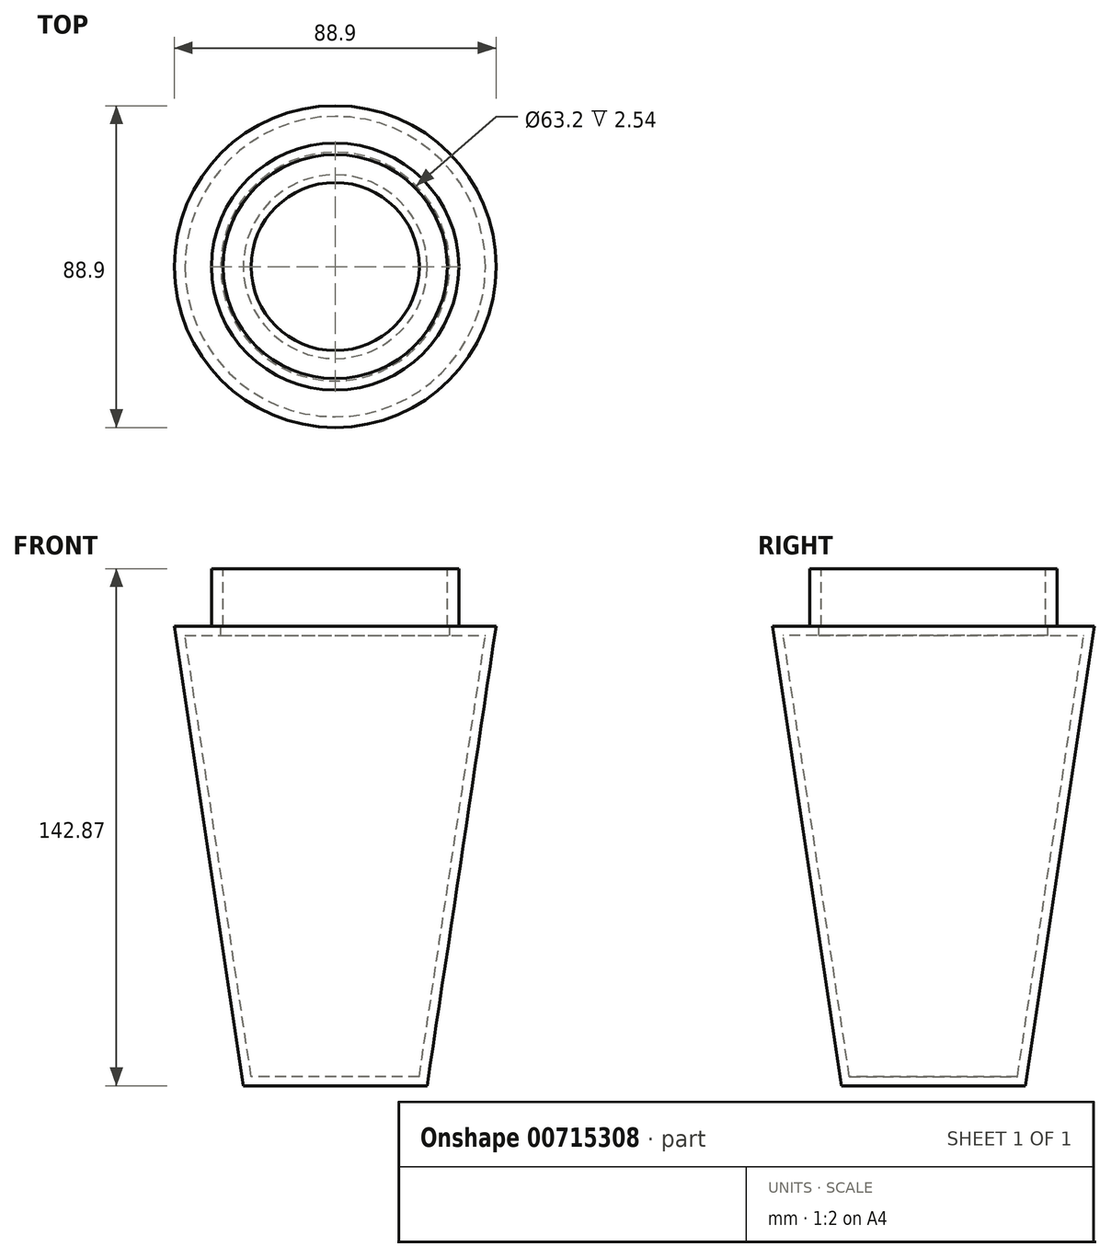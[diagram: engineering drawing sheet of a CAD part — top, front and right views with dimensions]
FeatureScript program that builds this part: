
annotation { "Feature Type Name" : "Feature", "Feature Type Description" : "" }
export const myFeature = defineFeature(function(context is Context, id is Id, definition is map)
    precondition{}
    {
        {
            var Q0;
            Q0=qCreatedBy(makeId("Front.planeOp"),FACE);
            var sketch = newSketch(context, id + "F0", { "sketchPlane" : qUnion([Q0])});
            skLineSegment(sketch, "E0", {"start": v(0, 49.63) * mm, "end": v(0, -84.13) * mm});
            skLineSegment(sketch, "E1", {"start": v(0, -84.13) * mm, "end": v(-25.4, -84.13) * mm});
            skLineSegment(sketch, "E2", {"start": v(-25.4, -84.13) * mm, "end": v(-44.45, 42.87) * mm});
            skLineSegment(sketch, "E3", {"start": v(-44.45, 42.87) * mm, "end": v(0, 42.87) * mm});
            skLineSegment(sketch, "E4", {"start": v(-34.14, 42.87) * mm, "end": v(-34.14, 58.74) * mm});
            skLineSegment(sketch, "E5", {"start": v(-34.14, 58.74) * mm, "end": v(-30.96, 58.74) * mm});
            skLineSegment(sketch, "E6", {"start": v(-30.96, 58.74) * mm, "end": v(-30.96, 42.87) * mm});
            skSolve(sketch);
        }
        {
            var Q0;
            Q0 = qSketchRegion(id + "F0", true);
            var Q1;
            Q1=sQuery(id+"F0.wireOp",EDGE,"E0");
            revolve(context, id + "F1", {"surfaceOperationType" : NewSurfaceOperationType.NEW, "entities" : qUnion([Q0]), "axis" : qUnion([Q1]), "revolveType" : RevolveType.FULL});
        }
        {
            var Q0;
            {var subQ0=sQuery(id+"F0.wireOp",EDGE,"E3");Q0=makeQuery(id+"F1.opRevolve","SWEPT_FACE",FACE,{"disambiguationData":[OSD([subQ0]),TDD([makeQuery(id+"F0.imprint","IMPRINT",EDGE,{"disambiguationData":[TD([[makeQuery(id+"F0.imprint","INTERSECT",VERTEX,{"derivedFrom":[sQuery(id+"F0.wireOp",EDGE,"E0"),subQ0]}),1.0]])],"derivedFrom":subQ0})])]});}
            shell(context, id + "F2", {"entities" : qUnion([Q0]), "thickness" : 2.54 * mm});
        }
    });
